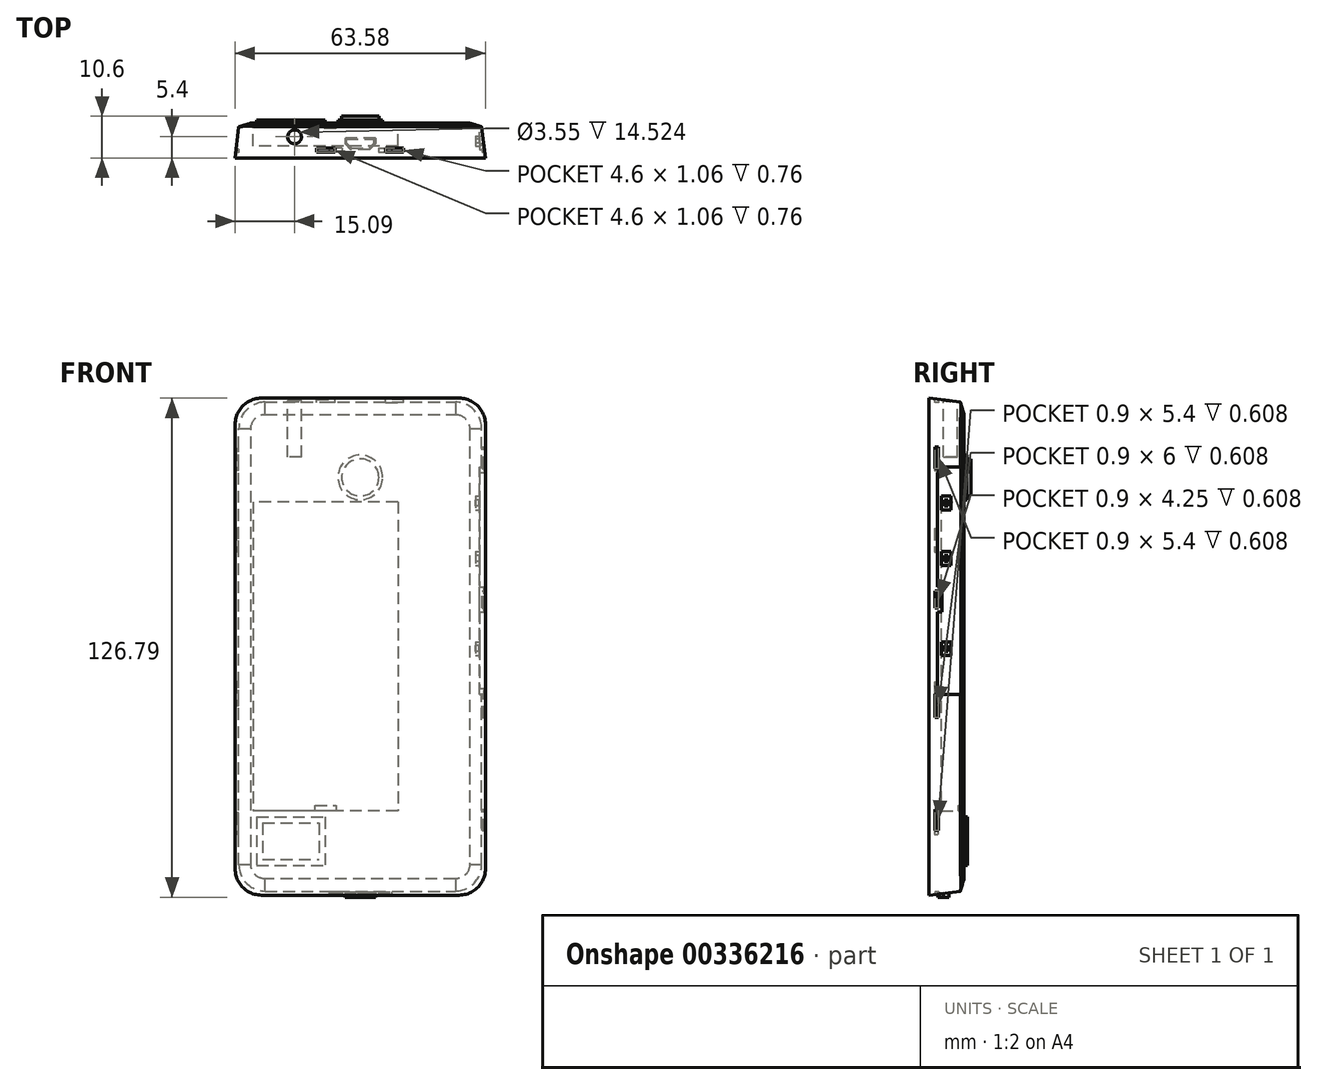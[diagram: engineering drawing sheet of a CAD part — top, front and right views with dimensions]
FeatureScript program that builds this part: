
annotation { "Feature Type Name" : "Feature", "Feature Type Description" : "" }
export const myFeature = defineFeature(function(context is Context, id is Id, definition is map)
    precondition{}
    {
        {
            var Q0;
            Q0=qCreatedBy(makeId("Front.planeOp"),FACE);
            cPlane(context, id + "F0", {"entities" : qUnion([Q0]), "cplaneType" : CPlaneType.OFFSET, "offset" : 9 * mm, "width" : 150 * mm, "height" : 150 * mm});
        }
        {
            var Q0;
            Q0=qCreatedBy(id+"F0.planeOp",FACE);
            var sketch = newSketch(context, id + "F1", { "sketchPlane" : qUnion([Q0])});
            skLineSegment(sketch, "E0.bottom", {"start": v(31.8, 63.15) * mm, "end": v(-31.8, 63.15) * mm});
            skLineSegment(sketch, "E0.top", {"start": v(31.8, -63.15) * mm, "end": v(-31.8, -63.15) * mm});
            skLineSegment(sketch, "E0.left", {"start": v(31.8, 63.15) * mm, "end": v(31.8, -63.15) * mm});
            skLineSegment(sketch, "E0.right", {"start": v(-31.8, 63.15) * mm, "end": v(-31.8, -63.15) * mm});
            skPoint(sketch, "E0.middle", {"position": v(0, 0) * mm});
            skLineSegment(sketch, "E1", {"start": v(0, -63.15) * mm, "end": v(0, -63.65) * mm, "construction": true});
            skPoint(sketch, "E1.endSnap0", {"position": v(0, -63.15) * mm});
            skSolve(sketch);
        }
        {
            var Q0;
            Q0=qCreatedBy(makeId("Front.planeOp"),FACE);
            var sketch = newSketch(context, id + "F2", { "sketchPlane" : qUnion([Q0])});
            skLineSegment(sketch, "E2.bottom", {"start": v(30.75, 62) * mm, "end": v(-30.75, 62) * mm});
            skLineSegment(sketch, "E2.top", {"start": v(30.75, -62) * mm, "end": v(-30.75, -62) * mm});
            skLineSegment(sketch, "E2.left", {"start": v(30.75, 62) * mm, "end": v(30.75, -62) * mm});
            skLineSegment(sketch, "E2.right", {"start": v(-30.75, 62) * mm, "end": v(-30.75, -62) * mm});
            skPoint(sketch, "E2.middle", {"position": v(0, 0) * mm});
            skSolve(sketch);
        }
        {
            var Q0;
            Q0 = qSketchRegion(id + "F1", true);
            var Q1;
            Q1 = qSketchRegion(id + "F2", true);
            loft(context, id + "F3", {"sheetProfilesArray" : [{ "sheetProfileEntities" : qUnion([Q0]) }, { "sheetProfileEntities" : qUnion([Q1]) }]});
        }
        {
            var Q0;
            Q0=makeQuery(id+"F3.opLoft","CAP_FACE",FACE,{"disambiguationData":[OSD([makeQuery(id+"F2.imprint","IMPRINT",FACE,{"disambiguationData":[TD([[makeQuery(id+"F2.imprint","IMPRINT",EDGE,{"derivedFrom":sQuery(id+"F2.wireOp",EDGE,"E2.bottom")}),1.0]])]})])],"isStart":true});
            var sketch = newSketch(context, id + "F4", { "sketchPlane" : qUnion([Q0])});
            skCircle(sketch, "E3", {"center": v(0, 43) * mm, "radius": 5.68 * mm});
            skSolve(sketch);
        }
        {
            var Q0;
            Q0 = qSketchRegion(id + "F4", true);
            extrude(context, id + "F5", {"entities" : qUnion([Q0]), "operationType" : NewBodyOperationType.ADD, "depth" : 0.75 * mm});
        }
        {
            var Q0;
            Q0=makeQuery(id+"F5.opExtrude","CAP_FACE",FACE,{"disambiguationData":[OSD([sQuery(id+"F4.wireOp",EDGE,"E3")])],"isStart":false});
            var sketch = newSketch(context, id + "F6", { "sketchPlane" : qUnion([Q0])});
            skCircle(sketch, "E4", {"center": v(0, 43) * mm, "radius": 4.72 * mm});
            skSolve(sketch);
        }
        {
            var Q0;
            Q0 = qSketchRegion(id + "F6", true);
            extrude(context, id + "F7", {"entities" : qUnion([Q0]), "operationType" : NewBodyOperationType.ADD, "depth" : 0.95 * mm});
        }
        {
            var Q0;
            Q0=makeQuery(id+"F3.opLoft","CAP_FACE",FACE,{"disambiguationData":[OSD([makeQuery(id+"F2.imprint","IMPRINT",FACE,{"disambiguationData":[TD([[makeQuery(id+"F2.imprint","IMPRINT",EDGE,{"derivedFrom":sQuery(id+"F2.wireOp",EDGE,"E2.bottom")}),1.0]])]})])],"isStart":true});
            var sketch = newSketch(context, id + "F8", { "sketchPlane" : qUnion([Q0])});
            skLineSegment(sketch, "E5.bottom", {"start": v(26.3, -43.3) * mm, "end": v(9, -43.3) * mm});
            skLineSegment(sketch, "E5.top", {"start": v(26.3, -55.6) * mm, "end": v(9, -55.6) * mm});
            skLineSegment(sketch, "E5.left", {"start": v(26.3, -43.3) * mm, "end": v(26.3, -55.6) * mm});
            skLineSegment(sketch, "E5.right", {"start": v(9, -43.3) * mm, "end": v(9, -55.6) * mm});
            skLineSegment(sketch, "E6", {"start": v(17.65, -43.3) * mm, "end": v(17.65, -55.6) * mm, "construction": true});
            skLineSegment(sketch, "E7.0", {"start": v(24.8, -44.8) * mm, "end": v(24.8, -54.1) * mm});
            skLineSegment(sketch, "E7.1", {"start": v(24.8, -44.8) * mm, "end": v(10.5, -44.8) * mm});
            skLineSegment(sketch, "E7.2", {"start": v(10.5, -44.8) * mm, "end": v(10.5, -54.1) * mm});
            skLineSegment(sketch, "E7.3", {"start": v(24.8, -54.1) * mm, "end": v(10.5, -54.1) * mm});
            skSolve(sketch);
        }
        {
            var Q0;
            Q0 = qSketchRegion(id + "F8", true);
            extrude(context, id + "F9", {"entities" : qUnion([Q0]), "operationType" : NewBodyOperationType.ADD, "depth" : 0.78 * mm});
        }
        {
            var Q0;
            Q0=sQuery(id+"F1.wireOp",VERTEX,"E1.end");
            var Q1;
            Q1=qCreatedBy(makeId("Top.planeOp"),FACE);
            cPlane(context, id + "F10", {"entities" : qUnion([Q0, Q1]), "cplaneType" : CPlaneType.PLANE_POINT, "offset" : 25 * mm, "width" : 150 * mm, "height" : 150 * mm});
        }
        {
            var Q0;
            Q0=qCreatedBy(id+"F10.planeOp",FACE);
            var sketch = newSketch(context, id + "F11", { "sketchPlane" : qUnion([Q0])});
            skLineSegment(sketch, "E8.bottom", {"start": v(-3.85, -6.7) * mm, "end": v(-2.4, -6.7) * mm, "construction": true});
            skLineSegment(sketch, "E8.top", {"start": v(-3.85, -3.8) * mm, "end": v(3.85, -3.8) * mm});
            skLineSegment(sketch, "E8.left", {"start": v(-3.85, -6.7) * mm, "end": v(-3.85, -5.25) * mm, "construction": true});
            skLineSegment(sketch, "E8.right", {"start": v(3.84, -6.7) * mm, "end": v(3.84, -5.25) * mm, "construction": true});
            skPoint(sketch, "E8.middle", {"position": v(0, -5.25) * mm});
            skLineSegment(sketch, "E9", {"start": v(-3.85, -5.25) * mm, "end": v(-2.4, -6.7) * mm});
            skLineSegment(sketch, "E10", {"start": v(0, -3.8) * mm, "end": v(0, -6.7) * mm, "construction": true});
            skLineSegment(sketch, "E11.MirrorCS", {"start": v(3.85, -5.25) * mm, "end": v(2.4, -6.7) * mm});
            skLineSegment(sketch, "E12", {"start": v(2.4, -6.7) * mm, "end": v(3.84, -6.7) * mm, "construction": true});
            skLineSegment(sketch, "E13", {"start": v(-2.4, -6.7) * mm, "end": v(2.4, -6.7) * mm});
            skLineSegment(sketch, "E14", {"start": v(3.84, -5.25) * mm, "end": v(3.84, -3.8) * mm});
            skLineSegment(sketch, "E15", {"start": v(-3.85, -5.25) * mm, "end": v(-3.85, -3.8) * mm});
            skLineSegment(sketch, "E16.0", {"start": v(-3.51, -5.11) * mm, "end": v(-3.51, -4.13) * mm});
            skLineSegment(sketch, "E16.1", {"start": v(3.51, -5.11) * mm, "end": v(3.51, -4.13) * mm});
            skLineSegment(sketch, "E16.2", {"start": v(3.51, -5.11) * mm, "end": v(2.26, -6.37) * mm});
            skLineSegment(sketch, "E16.3", {"start": v(-3.51, -4.13) * mm, "end": v(3.51, -4.13) * mm});
            skLineSegment(sketch, "E16.4", {"start": v(-2.26, -6.37) * mm, "end": v(2.26, -6.37) * mm});
            skLineSegment(sketch, "E16.5", {"start": v(-3.51, -5.11) * mm, "end": v(-2.26, -6.37) * mm});
            skSolve(sketch);
        }
        {
            var Q0;
            Q0 = qSketchRegion(id + "F11", true);
            extrude(context, id + "F12", {"entities" : qUnion([Q0]), "operationType" : NewBodyOperationType.ADD, "endBound" : BoundingType.UP_TO_NEXT, "depth" : 25 * mm});
        }
        {
            var Q0;
            Q0=qCreatedBy(makeId("Top.planeOp"),FACE);
            var Q1;
            Q1=makeQuery(id+"F3.opLoft","MID_CAP_VERTEX",VERTEX,{"disambiguationData":[OSD([sQuery(id+"F1.wireOp",EDGE,"E0.bottom"),sQuery(id+"F1.wireOp",EDGE,"E0.right")])],"capPos":0.0});
            cPlane(context, id + "F13", {"entities" : qUnion([Q0, Q1]), "cplaneType" : CPlaneType.PLANE_POINT, "offset" : 25 * mm, "width" : 150 * mm, "height" : 150 * mm});
        }
        {
            var Q0;
            Q0=qCreatedBy(id+"F13.planeOp",FACE);
            var sketch = newSketch(context, id + "F14", { "sketchPlane" : qUnion([Q0])});
            skCircle(sketch, "E17", {"center": v(-16.7, -3.5) * mm, "radius": 1.77 * mm});
            skSolve(sketch);
        }
        {
            var Q0;
            Q0 = qSketchRegion(id + "F14", true);
            extrude(context, id + "F15", {"entities" : qUnion([Q0]), "operationType" : NewBodyOperationType.REMOVE, "oppositeDirection" : true, "depth" : 15 * mm});
        }
        {
            var Q0;
            {var subQ6=sQuery(id+"F2.wireOp",EDGE,"E2.bottom");Q0=makeQuery(id+"F9.boolean.opBoolean","SPLIT",FACE,{"disambiguationData":[TD([makeQuery(id+"F5.opExtrude","SWEPT_FACE",FACE,{"disambiguationData":[OSD([sQuery(id+"F4.wireOp",EDGE,"E3")])]})])],"derivedFrom":makeQuery(id+"F3.opLoft","CAP_FACE",FACE,{"disambiguationData":[OSD([makeQuery(id+"F2.imprint","IMPRINT",FACE,{"disambiguationData":[TD([[makeQuery(id+"F2.imprint","IMPRINT",EDGE,{"derivedFrom":subQ6}),1.0]])]})])],"isStart":true})});}
            var sketch = newSketch(context, id + "F16", { "sketchPlane" : qUnion([Q0])});
            skLineSegment(sketch, "E18.bottom", {"start": v(-9.56, 36.8) * mm, "end": v(27.24, 36.8) * mm});
            skLineSegment(sketch, "E18.top", {"start": v(-9.56, -41.73) * mm, "end": v(27.24, -41.73) * mm});
            skLineSegment(sketch, "E18.left", {"start": v(-9.56, 36.8) * mm, "end": v(-9.56, -41.73) * mm});
            skLineSegment(sketch, "E18.right", {"start": v(27.24, 36.8) * mm, "end": v(27.24, -41.73) * mm});
            skSolve(sketch);
        }
        {
            var Q0;
            Q0 = qSketchRegion(id + "F16", true);
            extrude(context, id + "F17", {"entities" : qUnion([Q0]), "operationType" : NewBodyOperationType.REMOVE, "oppositeDirection" : true, "depth" : 5.84 * mm});
        }
        {
            var Q0;
            {var subQ6=sQuery(id+"F2.wireOp",EDGE,"E2.bottom");Q0=makeQuery(id+"F9.boolean.opBoolean","SPLIT",FACE,{"disambiguationData":[TD([makeQuery(id+"F5.opExtrude","SWEPT_FACE",FACE,{"disambiguationData":[OSD([sQuery(id+"F4.wireOp",EDGE,"E3")])]})])],"derivedFrom":makeQuery(id+"F3.opLoft","CAP_FACE",FACE,{"disambiguationData":[OSD([makeQuery(id+"F2.imprint","IMPRINT",FACE,{"disambiguationData":[TD([[makeQuery(id+"F2.imprint","IMPRINT",EDGE,{"derivedFrom":subQ6}),1.0]])]})])],"isStart":true})});}
            var sketch = newSketch(context, id + "F18", { "sketchPlane" : qUnion([Q0])});
            skLineSegment(sketch, "E19.0", {"start": v(6.2, -41.73) * mm, "end": v(11.5, -41.73) * mm});
            skLineSegment(sketch, "E20", {"start": v(11.5, -41.73) * mm, "end": v(11.5, -40.33) * mm});
            skLineSegment(sketch, "E21", {"start": v(11.5, -40.33) * mm, "end": v(6.2, -40.33) * mm});
            skLineSegment(sketch, "E22", {"start": v(6.2, -40.33) * mm, "end": v(6.2, -41.73) * mm});
            skPoint(sketch, "E23.orphan", {"position": v(-9.56, -41.73) * mm});
            skPoint(sketch, "E24.orphan", {"position": v(27.24, -41.73) * mm});
            skLineSegment(sketch, "E25", {"start": v(8.84, -40.33) * mm, "end": v(8.84, -41.73) * mm, "construction": true});
            skSolve(sketch);
        }
        {
            var Q0;
            Q0 = qSketchRegion(id + "F18", true);
            extrude(context, id + "F19", {"entities" : qUnion([Q0]), "operationType" : NewBodyOperationType.ADD, "oppositeDirection" : true, "depth" : 1.4 * mm});
        }
        {
            var Q0;
            Q0=qCreatedBy(makeId("Right.planeOp"),FACE);
            var Q1;
            Q1=makeQuery(id+"F3.opLoft","MID_CAP_VERTEX",VERTEX,{"disambiguationData":[OSD([sQuery(id+"F1.wireOp",EDGE,"E0.bottom"),sQuery(id+"F1.wireOp",EDGE,"E0.left")])],"capPos":0.0});
            cPlane(context, id + "F20", {"entities" : qUnion([Q0, Q1]), "cplaneType" : CPlaneType.PLANE_POINT, "offset" : 25 * mm, "width" : 150 * mm, "height" : 150 * mm});
        }
        {
            var Q0;
            Q0=qCreatedBy(id+"F20.planeOp",FACE);
            var sketch = newSketch(context, id + "F21", { "sketchPlane" : qUnion([Q0])});
            skLineSegment(sketch, "E26.0", {"start": v(0, 62) * mm, "end": v(0, -62) * mm});
            skLineSegment(sketch, "E27", {"start": v(0, 45.7) * mm, "end": v(-5.28, 45.7) * mm});
            skLineSegment(sketch, "E28", {"start": v(-6.78, 44.2) * mm, "end": v(-6.78, 15.2) * mm});
            skLineSegment(sketch, "E29", {"start": v(-5.28, -12.1) * mm, "end": v(0, -12.1) * mm});
            skLineSegment(sketch, "E30", {"start": v(-5.28, 45.7) * mm, "end": v(-6.78, 44.2) * mm});
            skLineSegment(sketch, "E31", {"start": v(-5.28, -12.1) * mm, "end": v(-6.78, -10.6) * mm});
            skLineSegment(sketch, "E32", {"start": v(-6.78, 8.8) * mm, "end": v(-5.67, 8.8) * mm});
            skLineSegment(sketch, "E33", {"start": v(-5.67, 8.8) * mm, "end": v(-5.67, 15.2) * mm});
            skLineSegment(sketch, "E34", {"start": v(-5.67, 15.2) * mm, "end": v(-6.78, 15.2) * mm});
            skPoint(sketch, "E35", {"position": v(-5.67, 12) * mm});
            skLineSegment(sketch, "E36.trimOffspring", {"start": v(-6.78, 8.8) * mm, "end": v(-6.78, -10.6) * mm});
            skSolve(sketch);
        }
        {
            var Q0;
            Q0 = qSketchRegion(id + "F21", true);
            extrude(context, id + "F22", {"entities" : qUnion([Q0]), "operationType" : NewBodyOperationType.REMOVE, "oppositeDirection" : true, "depth" : 1.5 * mm});
        }
        {
            var Q0;
            Q0=makeQuery(id+"F22.boolean.opBoolean","COPY",FACE,{"derivedFrom":makeQuery(id+"F22.opExtrude","CAP_FACE",FACE,{"disambiguationData":[OSD([sQuery(id+"F21.wireOp",EDGE,"E26.0"),sQuery(id+"F21.wireOp",EDGE,"E27"),sQuery(id+"F21.wireOp",EDGE,"E28"),sQuery(id+"F21.wireOp",EDGE,"E29")])],"isStart":false})});
            var sketch = newSketch(context, id + "F23", { "sketchPlane" : qUnion([Q0])});
            skLineSegment(sketch, "E37.bottom", {"start": v(-3.3, 38.25) * mm, "end": v(-5.8, 38.25) * mm});
            skLineSegment(sketch, "E37.top", {"start": v(-3.3, 34.75) * mm, "end": v(-5.8, 34.75) * mm});
            skLineSegment(sketch, "E37.left", {"start": v(-3.3, 38.25) * mm, "end": v(-3.3, 34.75) * mm});
            skLineSegment(sketch, "E37.right", {"start": v(-5.8, 38.25) * mm, "end": v(-5.8, 34.75) * mm});
            skLineSegment(sketch, "E38.bottom", {"start": v(-3.3, 24.15) * mm, "end": v(-5.8, 24.15) * mm});
            skLineSegment(sketch, "E38.top", {"start": v(-3.3, 20.65) * mm, "end": v(-5.8, 20.65) * mm});
            skLineSegment(sketch, "E38.left", {"start": v(-3.3, 24.15) * mm, "end": v(-3.3, 20.65) * mm});
            skLineSegment(sketch, "E38.right", {"start": v(-5.8, 24.15) * mm, "end": v(-5.8, 20.65) * mm});
            skLineSegment(sketch, "E39.bottom", {"start": v(-3.3, 1.25) * mm, "end": v(-5.8, 1.25) * mm});
            skLineSegment(sketch, "E39.top", {"start": v(-3.3, -2.25) * mm, "end": v(-5.8, -2.25) * mm});
            skLineSegment(sketch, "E39.left", {"start": v(-3.3, 1.25) * mm, "end": v(-3.3, -2.25) * mm});
            skLineSegment(sketch, "E39.right", {"start": v(-5.8, 1.25) * mm, "end": v(-5.8, -2.25) * mm});
            skLineSegment(sketch, "E40", {"start": v(-3.3, 36.5) * mm, "end": v(-5.8, 36.5) * mm, "construction": true});
            skLineSegment(sketch, "E41", {"start": v(-3.3, 22.4) * mm, "end": v(-5.8, 22.4) * mm, "construction": true});
            skLineSegment(sketch, "E42", {"start": v(-3.3, -0.5) * mm, "end": v(-5.8, -0.5) * mm, "construction": true});
            skSolve(sketch);
        }
        {
            var Q0;
            Q0 = qSketchRegion(id + "F23", true);
            extrude(context, id + "F24", {"entities" : qUnion([Q0]), "operationType" : NewBodyOperationType.REMOVE, "oppositeDirection" : true, "depth" : 1 * mm});
        }
        {
            var Q0;
            Q0=makeQuery(id+"F24.boolean.opBoolean","COPY",FACE,{"derivedFrom":makeQuery(id+"F24.opExtrude","CAP_FACE",FACE,{"disambiguationData":[OSD([sQuery(id+"F23.wireOp",EDGE,"E37.bottom"),sQuery(id+"F23.wireOp",EDGE,"E37.top"),sQuery(id+"F23.wireOp",EDGE,"E37.left"),sQuery(id+"F23.wireOp",EDGE,"E37.right")])],"isStart":false})});
            var sketch = newSketch(context, id + "F25", { "sketchPlane" : qUnion([Q0])});
            skLineSegment(sketch, "E43.bottom", {"start": v(-4.05, 35.75) * mm, "end": v(-5.05, 35.75) * mm});
            skLineSegment(sketch, "E43.top", {"start": v(-4.05, 37.25) * mm, "end": v(-5.05, 37.25) * mm});
            skLineSegment(sketch, "E43.left", {"start": v(-4.05, 35.75) * mm, "end": v(-4.05, 37.25) * mm});
            skLineSegment(sketch, "E43.right", {"start": v(-5.05, 35.75) * mm, "end": v(-5.05, 37.25) * mm});
            skPoint(sketch, "E43.middle", {"position": v(-4.55, 36.5) * mm});
            skPoint(sketch, "E43.middle.positionSnap0", {"position": v(-3.3, 36.5) * mm});
            skPoint(sketch, "E43.middle.positionSnap1", {"position": v(-4.55, 34.75) * mm});
            skPoint(sketch, "E43.centerSnap0", {"position": v(-3.3, 36.5) * mm});
            skPoint(sketch, "E43.centerSnap1", {"position": v(-4.55, 34.75) * mm});
            skPoint(sketch, "E44.0", {"position": v(-3.3, 22.4) * mm});
            skPoint(sketch, "E45.0", {"position": v(-3.3, -0.5) * mm});
            skLineSegment(sketch, "E46.bottom", {"start": v(-4.05, 23.15) * mm, "end": v(-5.05, 23.15) * mm});
            skLineSegment(sketch, "E46.top", {"start": v(-4.05, 21.65) * mm, "end": v(-5.05, 21.65) * mm});
            skLineSegment(sketch, "E46.left", {"start": v(-4.05, 23.15) * mm, "end": v(-4.05, 21.65) * mm});
            skLineSegment(sketch, "E46.right", {"start": v(-5.05, 23.15) * mm, "end": v(-5.05, 21.65) * mm});
            skPoint(sketch, "E46.middle", {"position": v(-4.55, 22.4) * mm});
            skLineSegment(sketch, "E47.bottom", {"start": v(-4.05, -1.25) * mm, "end": v(-5.05, -1.25) * mm});
            skLineSegment(sketch, "E47.top", {"start": v(-4.05, 0.25) * mm, "end": v(-5.05, 0.25) * mm});
            skLineSegment(sketch, "E47.left", {"start": v(-4.05, -1.25) * mm, "end": v(-4.05, 0.25) * mm});
            skLineSegment(sketch, "E47.right", {"start": v(-5.05, -1.25) * mm, "end": v(-5.05, 0.25) * mm});
            skPoint(sketch, "E47.middle", {"position": v(-4.55, -0.5) * mm});
            skSolve(sketch);
        }
        {
            var Q0;
            Q0 = qSketchRegion(id + "F25", true);
            extrude(context, id + "F26", {"entities" : qUnion([Q0]), "operationType" : NewBodyOperationType.ADD, "depth" : 0.85 * mm});
        }
        {
            var Q0;
            Q0=qCreatedBy(id+"F20.planeOp",FACE);
            var sketch = newSketch(context, id + "F27", { "sketchPlane" : qUnion([Q0])});
            skLineSegment(sketch, "E48.bottom", {"start": v(-6.5, 45.3) * mm, "end": v(-7.4, 45.3) * mm});
            skLineSegment(sketch, "E48.top", {"start": v(-6.5, 50.7) * mm, "end": v(-7.4, 50.7) * mm});
            skLineSegment(sketch, "E48.left", {"start": v(-6.5, 45.3) * mm, "end": v(-6.5, 50.7) * mm});
            skLineSegment(sketch, "E48.right", {"start": v(-7.4, 45.3) * mm, "end": v(-7.4, 50.7) * mm});
            skPoint(sketch, "E48.middle", {"position": v(-6.95, 48) * mm});
            skLineSegment(sketch, "E49.bottom", {"start": v(-6.5, 9.87) * mm, "end": v(-7.4, 9.87) * mm});
            skLineSegment(sketch, "E49.top", {"start": v(-6.5, 14.12) * mm, "end": v(-7.4, 14.12) * mm});
            skLineSegment(sketch, "E49.left", {"start": v(-6.5, 9.87) * mm, "end": v(-6.5, 14.12) * mm});
            skLineSegment(sketch, "E49.right", {"start": v(-7.4, 9.87) * mm, "end": v(-7.4, 14.12) * mm});
            skPoint(sketch, "E49.middle", {"position": v(-6.95, 12) * mm});
            skLineSegment(sketch, "E50.bottom", {"start": v(-6.5, -18) * mm, "end": v(-7.4, -18) * mm});
            skLineSegment(sketch, "E50.top", {"start": v(-6.5, -12) * mm, "end": v(-7.4, -12) * mm});
            skLineSegment(sketch, "E50.left", {"start": v(-6.5, -18) * mm, "end": v(-6.5, -12) * mm});
            skLineSegment(sketch, "E50.right", {"start": v(-7.4, -18) * mm, "end": v(-7.4, -12) * mm});
            skPoint(sketch, "E50.middle", {"position": v(-6.95, -15) * mm});
            skLineSegment(sketch, "E51.bottom", {"start": v(-6.5, -46.7) * mm, "end": v(-7.4, -46.7) * mm});
            skLineSegment(sketch, "E51.top", {"start": v(-6.5, -41.3) * mm, "end": v(-7.4, -41.3) * mm});
            skLineSegment(sketch, "E51.left", {"start": v(-6.5, -46.7) * mm, "end": v(-6.5, -41.3) * mm});
            skLineSegment(sketch, "E51.right", {"start": v(-7.4, -46.7) * mm, "end": v(-7.4, -41.3) * mm});
            skPoint(sketch, "E51.middle", {"position": v(-6.95, -44) * mm});
            skSolve(sketch);
        }
        {
            var Q0;
            Q0 = qSketchRegion(id + "F27", true);
            extrude(context, id + "F28", {"entities" : qUnion([Q0]), "operationType" : NewBodyOperationType.REMOVE, "oppositeDirection" : true, "depth" : 0.9 * mm});
        }
        {
            var Q0;
            Q0=qCreatedBy(makeId("Right.planeOp"),FACE);
            var Q1;
            Q1=makeQuery(id+"F3.opLoft","MID_CAP_VERTEX",VERTEX,{"disambiguationData":[OSD([sQuery(id+"F1.wireOp",EDGE,"E0.bottom"),sQuery(id+"F1.wireOp",EDGE,"E0.right")])],"capPos":0.0});
            cPlane(context, id + "F29", {"entities" : qUnion([Q0, Q1]), "cplaneType" : CPlaneType.PLANE_POINT, "offset" : 25 * mm, "width" : 150 * mm, "height" : 150 * mm});
        }
        {
            var Q0;
            Q0=qCreatedBy(id+"F29.planeOp",FACE);
            var sketch = newSketch(context, id + "F30", { "sketchPlane" : qUnion([Q0])});
            skLineSegment(sketch, "E52.bottom", {"start": v(-6.6, 44.8) * mm, "end": v(-7.5, 44.8) * mm});
            skLineSegment(sketch, "E52.top", {"start": v(-6.6, 50.2) * mm, "end": v(-7.5, 50.2) * mm});
            skLineSegment(sketch, "E52.left", {"start": v(-6.6, 44.8) * mm, "end": v(-6.6, 50.2) * mm});
            skLineSegment(sketch, "E52.right", {"start": v(-7.5, 44.8) * mm, "end": v(-7.5, 50.2) * mm});
            skPoint(sketch, "E52.middle", {"position": v(-7.05, 47.5) * mm});
            skLineSegment(sketch, "E53.bottom", {"start": v(-6.6, 24) * mm, "end": v(-7.5, 24) * mm});
            skLineSegment(sketch, "E53.top", {"start": v(-6.6, 30) * mm, "end": v(-7.5, 30) * mm});
            skLineSegment(sketch, "E53.left", {"start": v(-6.6, 24) * mm, "end": v(-6.6, 30) * mm});
            skLineSegment(sketch, "E53.right", {"start": v(-7.5, 24) * mm, "end": v(-7.5, 30) * mm});
            skPoint(sketch, "E53.middle", {"position": v(-7.05, 27) * mm});
            skLineSegment(sketch, "E54.bottom", {"start": v(-6.6, -15.05) * mm, "end": v(-7.5, -15.05) * mm});
            skLineSegment(sketch, "E54.top", {"start": v(-6.6, -8.95) * mm, "end": v(-7.5, -8.95) * mm});
            skLineSegment(sketch, "E54.left", {"start": v(-6.6, -15.05) * mm, "end": v(-6.6, -8.95) * mm});
            skLineSegment(sketch, "E54.right", {"start": v(-7.5, -15.05) * mm, "end": v(-7.5, -8.95) * mm});
            skPoint(sketch, "E54.middle", {"position": v(-7.05, -12) * mm});
            skPoint(sketch, "E54.middle.positionSnap0", {"position": v(-7.05, 24) * mm});
            skPoint(sketch, "E54.cornerSnap0", {"position": v(-6.6, 47.5) * mm});
            skPoint(sketch, "E54.centerSnap0", {"position": v(-7.05, 24) * mm});
            skLineSegment(sketch, "E55.bottom", {"start": v(-6.6, -47.75) * mm, "end": v(-7.5, -47.75) * mm});
            skLineSegment(sketch, "E55.top", {"start": v(-6.6, -42.25) * mm, "end": v(-7.5, -42.25) * mm});
            skLineSegment(sketch, "E55.left", {"start": v(-6.6, -47.75) * mm, "end": v(-6.6, -42.25) * mm});
            skLineSegment(sketch, "E55.right", {"start": v(-7.5, -47.75) * mm, "end": v(-7.5, -42.25) * mm});
            skPoint(sketch, "E55.middle", {"position": v(-7.05, -45) * mm});
            skSolve(sketch);
        }
        {
            var Q0;
            Q0 = qSketchRegion(id + "F30", true);
            extrude(context, id + "F31", {"entities" : qUnion([Q0]), "operationType" : NewBodyOperationType.REMOVE, "depth" : 0.9 * mm});
        }
        {
            var Q0;
            Q0=qCreatedBy(makeId("Top.planeOp"),FACE);
            var Q1;
            Q1=makeQuery(id+"F3.opLoft","MID_CAP_VERTEX",VERTEX,{"disambiguationData":[OSD([sQuery(id+"F1.wireOp",EDGE,"E0.top"),sQuery(id+"F1.wireOp",EDGE,"E0.right")])],"capPos":0.0});
            cPlane(context, id + "F32", {"entities" : qUnion([Q0, Q1]), "cplaneType" : CPlaneType.PLANE_POINT, "offset" : 25 * mm, "width" : 150 * mm, "height" : 150 * mm});
        }
        {
            var Q0;
            Q0=qCreatedBy(id+"F32.planeOp",FACE);
            var sketch = newSketch(context, id + "F33", { "sketchPlane" : qUnion([Q0])});
            skLineSegment(sketch, "E56.bottom", {"start": v(4.6, -6.37) * mm, "end": v(7.9, -6.37) * mm});
            skLineSegment(sketch, "E56.top", {"start": v(4.6, -7.37) * mm, "end": v(7.9, -7.37) * mm});
            skLineSegment(sketch, "E56.left", {"start": v(4.6, -6.37) * mm, "end": v(4.6, -7.37) * mm});
            skLineSegment(sketch, "E56.right", {"start": v(7.9, -6.37) * mm, "end": v(7.9, -7.37) * mm});
            skPoint(sketch, "E56.middle", {"position": v(6.25, -6.87) * mm});
            skPoint(sketch, "E57.0", {"position": v(0, 0) * mm});
            skLineSegment(sketch, "E58", {"start": v(0, 0) * mm, "end": v(0, -3.54) * mm, "construction": true});
            skPoint(sketch, "E59.MirrorP", {"position": v(-6.25, -6.87) * mm});
            skLineSegment(sketch, "E60.MirrorCS", {"start": v(-4.6, -6.37) * mm, "end": v(-4.6, -7.37) * mm});
            skLineSegment(sketch, "E61.MirrorCS", {"start": v(-7.9, -6.37) * mm, "end": v(-7.9, -7.37) * mm});
            skLineSegment(sketch, "E62.MirrorCS", {"start": v(-4.6, -7.37) * mm, "end": v(-7.9, -7.37) * mm});
            skLineSegment(sketch, "E63.MirrorCS", {"start": v(-4.6, -6.37) * mm, "end": v(-7.9, -6.37) * mm});
            skSolve(sketch);
        }
        {
            var Q0;
            Q0 = qSketchRegion(id + "F33", true);
            extrude(context, id + "F34", {"entities" : qUnion([Q0]), "operationType" : NewBodyOperationType.REMOVE, "depth" : .9 * mm});
        }
        {
            var Q0;
            Q0=qCreatedBy(makeId("Top.planeOp"),FACE);
            var Q1;
            Q1=makeQuery(id+"F3.opLoft","MID_CAP_VERTEX",VERTEX,{"disambiguationData":[OSD([sQuery(id+"F1.wireOp",EDGE,"E0.bottom"),sQuery(id+"F1.wireOp",EDGE,"E0.left")])],"capPos":0.0});
            cPlane(context, id + "F35", {"entities" : qUnion([Q0, Q1]), "cplaneType" : CPlaneType.PLANE_POINT, "offset" : 25 * mm, "width" : 150 * mm, "height" : 150 * mm});
        }
        {
            var Q0;
            Q0=qCreatedBy(id+"F35.planeOp",FACE);
            var sketch = newSketch(context, id + "F36", { "sketchPlane" : qUnion([Q0])});
            skLineSegment(sketch, "E64.bottom", {"start": v(-6.45, -6.34) * mm, "end": v(-11.05, -6.34) * mm});
            skLineSegment(sketch, "E64.top", {"start": v(-6.45, -7.4) * mm, "end": v(-11.05, -7.4) * mm});
            skLineSegment(sketch, "E64.left", {"start": v(-6.45, -6.34) * mm, "end": v(-6.45, -7.4) * mm});
            skLineSegment(sketch, "E64.right", {"start": v(-11.05, -6.34) * mm, "end": v(-11.05, -7.4) * mm});
            skPoint(sketch, "E64.middle", {"position": v(-8.75, -6.87) * mm});
            skLineSegment(sketch, "E65", {"start": v(0, 0) * mm, "end": v(0, -6.87) * mm, "construction": true});
            skPoint(sketch, "E66.MirrorP", {"position": v(8.75, -6.87) * mm});
            skLineSegment(sketch, "E67.MirrorCS", {"start": v(6.45, -6.34) * mm, "end": v(11.05, -6.34) * mm});
            skLineSegment(sketch, "E68.MirrorCS", {"start": v(6.45, -6.34) * mm, "end": v(6.45, -7.4) * mm});
            skLineSegment(sketch, "E69.MirrorCS", {"start": v(11.05, -6.34) * mm, "end": v(11.05, -7.4) * mm});
            skLineSegment(sketch, "E70.MirrorCS", {"start": v(6.45, -7.4) * mm, "end": v(11.05, -7.4) * mm});
            skSolve(sketch);
        }
        {
            var Q0;
            Q0 = qSketchRegion(id + "F36", true);
            extrude(context, id + "F37", {"entities" : qUnion([Q0]), "operationType" : NewBodyOperationType.REMOVE, "oppositeDirection" : true, "depth" : 1.1 * mm});
        }
        {
            var Q0;
            Q0=makeQuery(id+"F3.opLoft","SWEPT_EDGE",EDGE,{"disambiguationData":[OSD([sQuery(id+"F1.wireOp",EDGE,"E0.bottom"),sQuery(id+"F1.wireOp",EDGE,"E0.left"),sQuery(id+"F2.wireOp",EDGE,"E2.bottom"),sQuery(id+"F2.wireOp",EDGE,"E2.left")])]});
            var Q1;
            Q1=makeQuery(id+"F3.opLoft","SWEPT_EDGE",EDGE,{"disambiguationData":[OSD([sQuery(id+"F1.wireOp",EDGE,"E0.bottom"),sQuery(id+"F1.wireOp",EDGE,"E0.right"),sQuery(id+"F2.wireOp",EDGE,"E2.bottom"),sQuery(id+"F2.wireOp",EDGE,"E2.right")])]});
            var Q2;
            Q2=makeQuery(id+"F3.opLoft","SWEPT_EDGE",EDGE,{"disambiguationData":[OSD([sQuery(id+"F1.wireOp",EDGE,"E0.top"),sQuery(id+"F1.wireOp",EDGE,"E0.left"),sQuery(id+"F2.wireOp",EDGE,"E2.top"),sQuery(id+"F2.wireOp",EDGE,"E2.left")])]});
            var Q3;
            Q3=makeQuery(id+"F3.opLoft","SWEPT_EDGE",EDGE,{"disambiguationData":[OSD([sQuery(id+"F1.wireOp",EDGE,"E0.top"),sQuery(id+"F1.wireOp",EDGE,"E0.right"),sQuery(id+"F2.wireOp",EDGE,"E2.top"),sQuery(id+"F2.wireOp",EDGE,"E2.right")])]});
            fillet(context, id + "F38", {"entities" : qUnion([Q0, Q1, Q2, Q3]), "radius" : 6.75 * mm, "tangentPropagation" : true, "allowEdgeOverflow" : false});
        }
        {
            var Q0;
            Q0=makeQuery(id+"F3.opLoft","MID_CAP_EDGE",EDGE,{"disambiguationData":[OSD([sQuery(id+"F2.wireOp",EDGE,"E2.bottom"),sQuery(id+"F2.wireOp",EDGE,"E2.top"),sQuery(id+"F2.wireOp",EDGE,"E2.right")])],"capPos":1.0});
            chamfer(context, id + "F39", {"entities" : qUnion([Q0]), "chamferType" : ChamferType.TWO_OFFSETS, "width1" : 3 * mm, "oppositeDirection" : false, "width2" : 1 * mm, "tangentPropagation" : true});
        }
        {
            var Q0;
            Q0=makeQuery(id+"F3.opLoft","CAP_FACE",FACE,{"disambiguationData":[OSD([makeQuery(id+"F1.imprint","IMPRINT",FACE,{"disambiguationData":[TD([[makeQuery(id+"F1.imprint","IMPRINT",EDGE,{"derivedFrom":sQuery(id+"F1.wireOp",EDGE,"E0.bottom")}),1.0]])]})])],"isStart":true});
            var sketch = newSketch(context, id + "F40", { "sketchPlane" : qUnion([Q0])});
            skFitSpline(sketch, "E71.0", {"points": [v(-21.84, 51.15) * mm, v(-20.9, 51.85) * mm, v(-20.11, 52.72) * mm, v(-19.52, 53.73) * mm, v(-19.13, 54.85) * mm, v(-18.97, 56.01) * mm, v(-19.04, 57.2) * mm, v(-19.35, 58.35) * mm, v(-19.86, 59.42) * mm, v(-20.58, 60.38) * mm, v(-21.47, 61.19) * mm, v(-22.5, 61.8) * mm, v(-23.62, 62.2) * mm, v(-24.79, 62.38) * mm, v(-25.96, 62.33) * mm, v(-27.11, 62.04) * mm, v(-28.17, 61.54) * mm, v(-29.11, 60.84) * mm, v(-29.9, 59.97) * mm, v(-30.49, 58.96) * mm, v(-30.87, 57.84) * mm, v(-31.03, 56.68) * mm, v(-30.96, 55.5) * mm, v(-30.66, 54.34) * mm, v(-30.14, 53.27) * mm, v(-29.43, 52.3) * mm, v(-28.54, 51.5) * mm, v(-27.52, 50.9) * mm, v(-26.4, 50.49) * mm, v(-25.22, 50.31) * mm, v(-24.04, 50.36) * mm, v(-22.9, 50.65) * mm, v(-21.84, 51.15) * mm, v(-20.9, 51.85) * mm, v(-20.11, 52.72) * mm]});
            skLineSegment(sketch, "E71.1", {"start": v(-31, -56.45) * mm, "end": v(-31, 56.45) * mm});
            skLineSegment(sketch, "E71.2", {"start": v(-25.1, 62.35) * mm, "end": v(25.1, 62.35) * mm});
            skFitSpline(sketch, "E71.3", {"points": [v(-29.9, -59.97) * mm, v(-29.11, -60.84) * mm, v(-28.17, -61.54) * mm, v(-27.11, -62.04) * mm, v(-25.96, -62.33) * mm, v(-24.79, -62.38) * mm, v(-23.62, -62.2) * mm, v(-22.5, -61.8) * mm, v(-21.47, -61.19) * mm, v(-20.58, -60.38) * mm, v(-19.86, -59.42) * mm, v(-19.35, -58.35) * mm, v(-19.04, -57.2) * mm, v(-18.97, -56.01) * mm, v(-19.13, -54.85) * mm, v(-19.52, -53.73) * mm, v(-20.11, -52.72) * mm, v(-20.9, -51.85) * mm, v(-21.84, -51.15) * mm, v(-22.9, -50.65) * mm, v(-24.04, -50.36) * mm, v(-25.22, -50.31) * mm, v(-26.4, -50.49) * mm, v(-27.52, -50.9) * mm, v(-28.54, -51.5) * mm, v(-29.43, -52.3) * mm, v(-30.14, -53.27) * mm, v(-30.66, -54.34) * mm, v(-30.96, -55.5) * mm, v(-31.03, -56.68) * mm, v(-30.87, -57.84) * mm, v(-30.49, -58.96) * mm, v(-29.9, -59.97) * mm, v(-29.11, -60.84) * mm, v(-28.17, -61.54) * mm]});
            skFitSpline(sketch, "E71.4", {"points": [v(29.9, 59.97) * mm, v(29.11, 60.84) * mm, v(28.17, 61.54) * mm, v(27.11, 62.04) * mm, v(25.96, 62.33) * mm, v(24.79, 62.38) * mm, v(23.62, 62.2) * mm, v(22.5, 61.8) * mm, v(21.47, 61.19) * mm, v(20.58, 60.38) * mm, v(19.86, 59.42) * mm, v(19.35, 58.35) * mm, v(19.04, 57.2) * mm, v(18.97, 56.01) * mm, v(19.13, 54.85) * mm, v(19.52, 53.73) * mm, v(20.11, 52.72) * mm, v(20.9, 51.85) * mm, v(21.84, 51.15) * mm, v(22.9, 50.65) * mm, v(24.04, 50.36) * mm, v(25.22, 50.31) * mm, v(26.4, 50.49) * mm, v(27.52, 50.9) * mm, v(28.54, 51.5) * mm, v(29.43, 52.3) * mm, v(30.14, 53.27) * mm, v(30.66, 54.34) * mm, v(30.96, 55.5) * mm, v(31.03, 56.68) * mm, v(30.87, 57.84) * mm, v(30.49, 58.96) * mm, v(29.9, 59.97) * mm, v(29.11, 60.84) * mm, v(28.17, 61.54) * mm]});
            skLineSegment(sketch, "E71.5", {"start": v(31, -56.45) * mm, "end": v(31, 56.45) * mm});
            skFitSpline(sketch, "E71.6", {"points": [v(21.84, -51.15) * mm, v(20.9, -51.85) * mm, v(20.11, -52.72) * mm, v(19.52, -53.73) * mm, v(19.13, -54.85) * mm, v(18.97, -56.01) * mm, v(19.04, -57.2) * mm, v(19.35, -58.35) * mm, v(19.86, -59.42) * mm, v(20.58, -60.38) * mm, v(21.47, -61.19) * mm, v(22.5, -61.8) * mm, v(23.62, -62.2) * mm, v(24.79, -62.38) * mm, v(25.96, -62.33) * mm, v(27.11, -62.04) * mm, v(28.17, -61.54) * mm, v(29.11, -60.84) * mm, v(29.9, -59.97) * mm, v(30.49, -58.96) * mm, v(30.87, -57.84) * mm, v(31.03, -56.68) * mm, v(30.96, -55.5) * mm, v(30.66, -54.34) * mm, v(30.14, -53.27) * mm, v(29.43, -52.3) * mm, v(28.54, -51.5) * mm, v(27.52, -50.9) * mm, v(26.4, -50.49) * mm, v(25.22, -50.31) * mm, v(24.04, -50.36) * mm, v(22.9, -50.65) * mm, v(21.84, -51.15) * mm, v(20.9, -51.85) * mm, v(20.11, -52.72) * mm]});
            skLineSegment(sketch, "E71.7", {"start": v(-25.1, -62.35) * mm, "end": v(25.1, -62.35) * mm});
            skLineSegment(sketch, "E72.bottom", {"start": v(37.5, 67.5) * mm, "end": v(-37.5, 67.5) * mm});
            skLineSegment(sketch, "E72.top", {"start": v(37.5, -67.5) * mm, "end": v(-37.5, -67.5) * mm});
            skLineSegment(sketch, "E72.left", {"start": v(37.5, 67.5) * mm, "end": v(37.5, -67.5) * mm});
            skLineSegment(sketch, "E72.right", {"start": v(-37.5, 67.5) * mm, "end": v(-37.5, -67.5) * mm});
            skPoint(sketch, "E72.middle", {"position": v(0, 0) * mm});
            skSolve(sketch);
        }
        {
            var Q0;
            Q0 = qSketchRegion(id + "F40", true);
            extrude(context, id + "F41", {"entities" : qUnion([Q0]), "operationType" : NewBodyOperationType.REMOVE, "oppositeDirection" : true, "depth" : .1 * mm});
        }
    });
